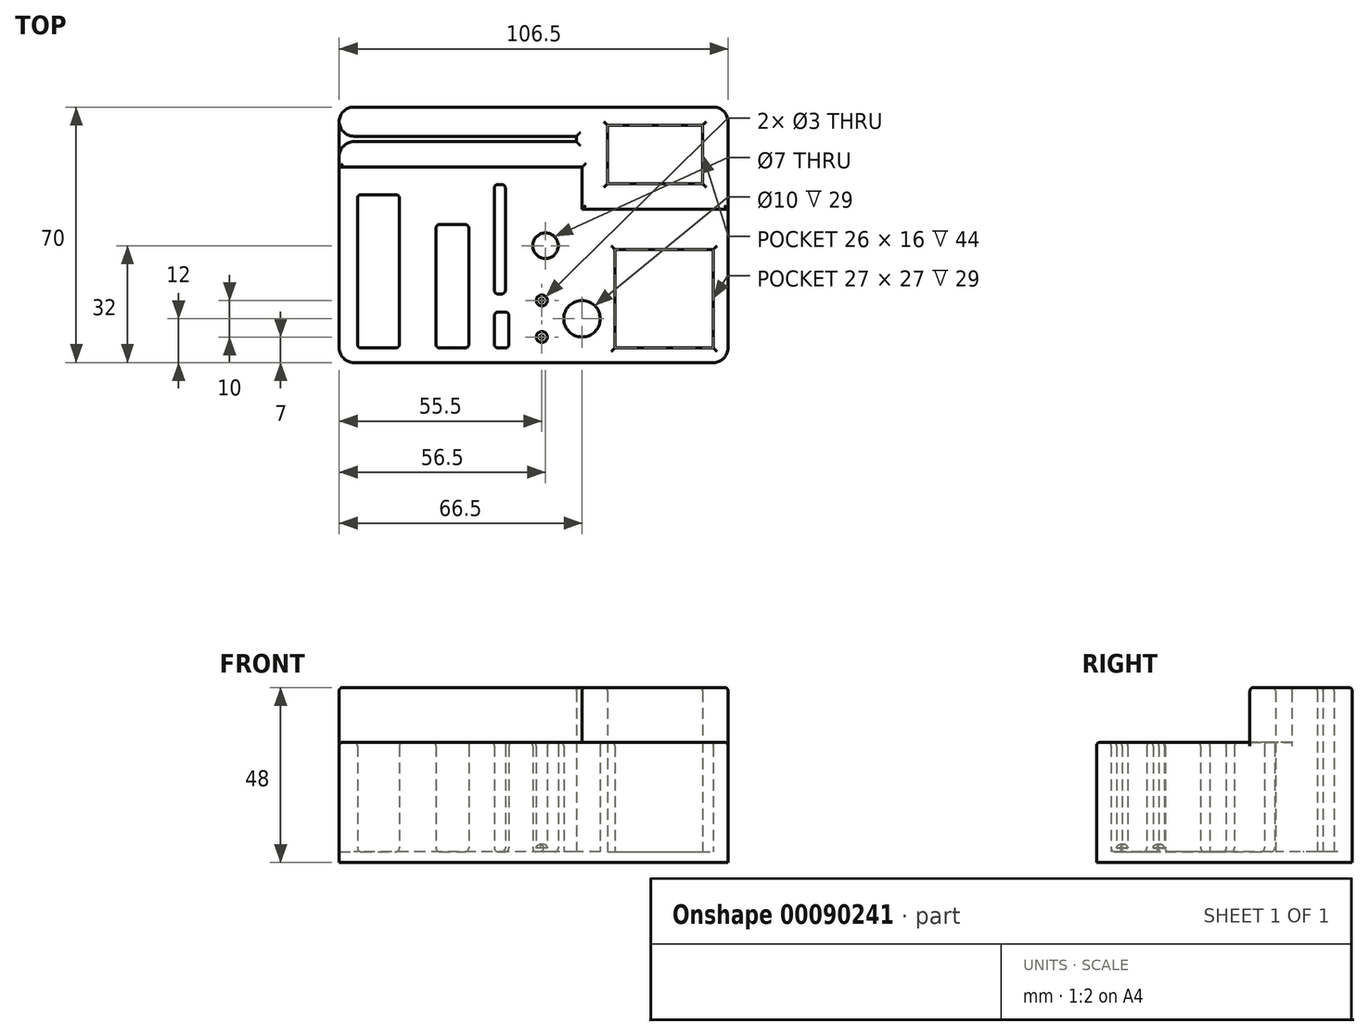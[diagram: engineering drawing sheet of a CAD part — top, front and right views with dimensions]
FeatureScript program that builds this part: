
annotation { "Feature Type Name" : "Feature", "Feature Type Description" : "" }
export const myFeature = defineFeature(function(context is Context, id is Id, definition is map)
    precondition{}
    {
        {
            var Q0;
            Q0=qCreatedBy(makeId("Top.planeOp"),FACE);
            var sketch = newSketch(context, id + "F0", { "sketchPlane" : qUnion([Q0])});
            skLineSegment(sketch, "E0.bottom", {"start": v(-53.25, 35) * mm, "end": v(53.25, 35) * mm});
            skLineSegment(sketch, "E0.top", {"start": v(-53.25, -35) * mm, "end": v(53.25, -35) * mm});
            skLineSegment(sketch, "E0.left", {"start": v(-53.25, 35) * mm, "end": v(-53.25, -35) * mm});
            skLineSegment(sketch, "E0.right", {"start": v(53.25, 35) * mm, "end": v(53.25, -35) * mm});
            skPoint(sketch, "E0.middle", {"position": v(0, 0) * mm});
            skSolve(sketch);
        }
        {
            var Q0;
            Q0 = qSketchRegion(id + "F0", true);
            extrude(context, id + "F1", {"entities" : qUnion([Q0]), "depth" : 3 * mm});
        }
        {
            var Q0;
            Q0=makeQuery(id+"F1.opExtrude","CAP_FACE",FACE,{"disambiguationData":[OSD([sQuery(id+"F0.wireOp",EDGE,"E0.bottom"),sQuery(id+"F0.wireOp",EDGE,"E0.top"),sQuery(id+"F0.wireOp",EDGE,"E0.left"),sQuery(id+"F0.wireOp",EDGE,"E0.right")])],"isStart":false});
            var sketch = newSketch(context, id + "F2", { "sketchPlane" : qUnion([Q0])});
            skLineSegment(sketch, "E1", {"start": v(-53.25, 27) * mm, "end": v(11.75, 27) * mm});
            skLineSegment(sketch, "E2", {"start": v(11.75, 27) * mm, "end": v(11.75, 25.5) * mm});
            skLineSegment(sketch, "E3", {"start": v(11.75, 25.5) * mm, "end": v(-53.25, 25.5) * mm});
            skLineSegment(sketch, "E4", {"start": v(-53.25, 27) * mm, "end": v(-53.25, 35) * mm});
            skLineSegment(sketch, "E5", {"start": v(-53.25, 35) * mm, "end": v(53.25, 35) * mm});
            skLineSegment(sketch, "E6", {"start": v(53.25, 35) * mm, "end": v(53.25, -35) * mm});
            skLineSegment(sketch, "E7", {"start": v(53.25, -35) * mm, "end": v(-53.25, -35) * mm});
            skLineSegment(sketch, "E8", {"start": v(-53.25, -35) * mm, "end": v(-53.25, 25.5) * mm});
            skLineSegment(sketch, "E9.bottom", {"start": v(-48.25, -31) * mm, "end": v(-36.75, -31) * mm});
            skLineSegment(sketch, "E9.top", {"start": v(-48.25, 11) * mm, "end": v(-36.75, 11) * mm});
            skLineSegment(sketch, "E9.left", {"start": v(-48.25, -31) * mm, "end": v(-48.25, 11) * mm});
            skLineSegment(sketch, "E9.right", {"start": v(-36.75, -31) * mm, "end": v(-36.75, 11) * mm});
            skLineSegment(sketch, "E10.bottom", {"start": v(-26.75, -31) * mm, "end": v(-17.75, -31) * mm});
            skLineSegment(sketch, "E10.top", {"start": v(-26.75, 2.8) * mm, "end": v(-17.75, 2.8) * mm});
            skLineSegment(sketch, "E10.left", {"start": v(-26.75, -31) * mm, "end": v(-26.75, 2.8) * mm});
            skLineSegment(sketch, "E10.right", {"start": v(-17.75, -31) * mm, "end": v(-17.75, 2.8) * mm});
            skLineSegment(sketch, "E11.bottom", {"start": v(-10.75, 13.8) * mm, "end": v(-7.75, 13.8) * mm});
            skLineSegment(sketch, "E11.top", {"start": v(-10.75, -16.2) * mm, "end": v(-7.75, -16.2) * mm});
            skLineSegment(sketch, "E11.left", {"start": v(-10.75, 13.8) * mm, "end": v(-10.75, -16.2) * mm});
            skLineSegment(sketch, "E11.right", {"start": v(-7.75, 13.8) * mm, "end": v(-7.75, -16.2) * mm});
            skLineSegment(sketch, "E12.bottom", {"start": v(-10.75, -31) * mm, "end": v(-6.75, -31) * mm});
            skLineSegment(sketch, "E12.top", {"start": v(-10.75, -21.2) * mm, "end": v(-6.75, -21.2) * mm});
            skLineSegment(sketch, "E12.left", {"start": v(-10.75, -31) * mm, "end": v(-10.75, -21.2) * mm});
            skLineSegment(sketch, "E12.right", {"start": v(-6.75, -31) * mm, "end": v(-6.75, -21.2) * mm});
            skCircle(sketch, "E13", {"center": v(3.25, -3) * mm, "radius": 3.5 * mm});
            skCircle(sketch, "E14", {"center": v(2.25, -18) * mm, "radius": 1.5 * mm});
            skCircle(sketch, "E15", {"center": v(2.25, -28) * mm, "radius": 1.5 * mm});
            skLineSegment(sketch, "E16.bottom", {"start": v(22.25, -4) * mm, "end": v(49.25, -4) * mm});
            skLineSegment(sketch, "E16.top", {"start": v(22.25, -31) * mm, "end": v(49.25, -31) * mm});
            skLineSegment(sketch, "E16.left", {"start": v(22.25, -4) * mm, "end": v(22.25, -31) * mm});
            skLineSegment(sketch, "E16.right", {"start": v(49.25, -4) * mm, "end": v(49.25, -31) * mm});
            skLineSegment(sketch, "E17.bottom", {"start": v(20.25, 30) * mm, "end": v(46.25, 30) * mm});
            skLineSegment(sketch, "E17.top", {"start": v(20.25, 14) * mm, "end": v(46.25, 14) * mm});
            skLineSegment(sketch, "E17.left", {"start": v(20.25, 30) * mm, "end": v(20.25, 14) * mm});
            skLineSegment(sketch, "E17.right", {"start": v(46.25, 30) * mm, "end": v(46.25, 14) * mm});
            skCircle(sketch, "E18", {"center": v(13.25, -23) * mm, "radius": 5 * mm});
            skLineSegment(sketch, "E19", {"start": v(53.25, 7) * mm, "end": v(13.25, 7) * mm});
            skLineSegment(sketch, "E20", {"start": v(13.25, 7) * mm, "end": v(13.25, 18.5) * mm});
            skLineSegment(sketch, "E21", {"start": v(13.25, 18.5) * mm, "end": v(-53.25, 18.5) * mm});
            skSolve(sketch);
        }
        {
            var Q0;
            {var subQ0=sQuery(id+"F2.wireOp",EDGE,"E7");Q0=makeQuery(id+"F2.imprint","IMPRINT",FACE,{"disambiguationData":[TD([[makeQuery(id+"F2.imprint","IMPRINT",EDGE,{"derivedFrom":subQ0}),1.0]])]});}
            extrude(context, id + "F3", {"entities" : qUnion([Q0]), "operationType" : NewBodyOperationType.ADD, "depth" : 30 * mm});
        }
        {
            var Q0;
            Q0=makeQuery(id+"F2.imprint","IMPRINT",FACE,{"disambiguationData":[TD([[makeQuery(id+"F2.imprint","IMPRINT",EDGE,{"derivedFrom":sQuery(id+"F2.wireOp",EDGE,"E1")}),1.0]])]});
            extrude(context, id + "F4", {"entities" : qUnion([Q0]), "operationType" : NewBodyOperationType.ADD, "depth" : 45 * mm});
        }
        {
            var Q0;
            Q0=makeQuery(id+"F3.opExtrude","CAP_EDGE",EDGE,{"disambiguationData":[OSD([sQuery(id+"F2.wireOp",EDGE,"E18")])],"isStart":false});
            var Q1;
            Q1=makeQuery(id+"F3.opExtrude","CAP_EDGE",EDGE,{"disambiguationData":[OSD([sQuery(id+"F2.wireOp",EDGE,"E16.bottom")])],"isStart":false});
            var Q2;
            Q2=makeQuery(id+"F3.opExtrude","CAP_EDGE",EDGE,{"disambiguationData":[OSD([sQuery(id+"F2.wireOp",EDGE,"E16.left")])],"isStart":false});
            var Q3;
            Q3=makeQuery(id+"F3.opExtrude","CAP_EDGE",EDGE,{"disambiguationData":[OSD([sQuery(id+"F2.wireOp",EDGE,"E16.right")])],"isStart":false});
            var Q4;
            Q4=makeQuery(id+"F3.opExtrude","CAP_EDGE",EDGE,{"disambiguationData":[OSD([sQuery(id+"F2.wireOp",EDGE,"E16.top")])],"isStart":false});
            var Q5;
            Q5=makeQuery(id+"F3.opExtrude","CAP_EDGE",EDGE,{"disambiguationData":[OSD([sQuery(id+"F2.wireOp",EDGE,"E14")])],"isStart":false});
            var Q6;
            Q6=makeQuery(id+"F3.opExtrude","CAP_EDGE",EDGE,{"disambiguationData":[OSD([sQuery(id+"F2.wireOp",EDGE,"E13")])],"isStart":false});
            var Q7;
            Q7=makeQuery(id+"F3.opExtrude","CAP_EDGE",EDGE,{"disambiguationData":[OSD([sQuery(id+"F2.wireOp",EDGE,"E15")])],"isStart":false});
            var Q8;
            Q8=makeQuery(id+"F3.opExtrude","CAP_EDGE",EDGE,{"disambiguationData":[OSD([sQuery(id+"F2.wireOp",EDGE,"E13")])],"isStart":true});
            var Q9;
            Q9=makeQuery(id+"F3.opExtrude","CAP_EDGE",EDGE,{"disambiguationData":[OSD([sQuery(id+"F2.wireOp",EDGE,"E15")])],"isStart":true});
            var Q10;
            Q10=makeQuery(id+"F3.opExtrude","CAP_EDGE",EDGE,{"disambiguationData":[OSD([sQuery(id+"F2.wireOp",EDGE,"E14")])],"isStart":true});
            var Q11;
            Q11=makeQuery(id+"F3.opExtrude","CAP_EDGE",EDGE,{"disambiguationData":[OSD([sQuery(id+"F2.wireOp",EDGE,"E11.right")])],"isStart":false});
            var Q12;
            Q12=makeQuery(id+"F3.opExtrude","CAP_EDGE",EDGE,{"disambiguationData":[OSD([sQuery(id+"F2.wireOp",EDGE,"E12.right")])],"isStart":false});
            var Q13;
            Q13=makeQuery(id+"F3.opExtrude","CAP_EDGE",EDGE,{"disambiguationData":[OSD([sQuery(id+"F2.wireOp",EDGE,"E11.left")])],"isStart":false});
            var Q14;
            Q14=makeQuery(id+"F3.opExtrude","CAP_EDGE",EDGE,{"disambiguationData":[OSD([sQuery(id+"F2.wireOp",EDGE,"E12.left")])],"isStart":false});
            var Q15;
            Q15=makeQuery(id+"F3.opExtrude","CAP_EDGE",EDGE,{"disambiguationData":[OSD([sQuery(id+"F2.wireOp",EDGE,"E11.bottom")])],"isStart":false});
            var Q16;
            Q16=makeQuery(id+"F3.opExtrude","SWEPT_EDGE",EDGE,{"disambiguationData":[OSD([sQuery(id+"F2.wireOp",EDGE,"E12.top"),sQuery(id+"F2.wireOp",EDGE,"E12.right")])]});
            var Q17;
            Q17=makeQuery(id+"F3.opExtrude","SWEPT_EDGE",EDGE,{"disambiguationData":[OSD([sQuery(id+"F2.wireOp",EDGE,"E11.top"),sQuery(id+"F2.wireOp",EDGE,"E11.right")])]});
            var Q18;
            Q18=makeQuery(id+"F3.opExtrude","CAP_EDGE",EDGE,{"disambiguationData":[OSD([sQuery(id+"F2.wireOp",EDGE,"E12.bottom")])],"isStart":false});
            var Q19;
            Q19=makeQuery(id+"F3.opExtrude","SWEPT_EDGE",EDGE,{"disambiguationData":[OSD([sQuery(id+"F2.wireOp",EDGE,"E12.top"),sQuery(id+"F2.wireOp",EDGE,"E12.left")])]});
            var Q20;
            Q20=makeQuery(id+"F3.opExtrude","CAP_EDGE",EDGE,{"disambiguationData":[OSD([sQuery(id+"F2.wireOp",EDGE,"E11.top")])],"isStart":false});
            var Q21;
            Q21=makeQuery(id+"F3.opExtrude","CAP_EDGE",EDGE,{"disambiguationData":[OSD([sQuery(id+"F2.wireOp",EDGE,"E12.top")])],"isStart":false});
            var Q22;
            Q22=makeQuery(id+"F3.opExtrude","CAP_EDGE",EDGE,{"disambiguationData":[OSD([sQuery(id+"F2.wireOp",EDGE,"E11.right")])],"isStart":true});
            var Q23;
            Q23=makeQuery(id+"F3.opExtrude","CAP_EDGE",EDGE,{"disambiguationData":[OSD([sQuery(id+"F2.wireOp",EDGE,"E12.bottom")])],"isStart":true});
            var Q24;
            Q24=makeQuery(id+"F3.opExtrude","SWEPT_EDGE",EDGE,{"disambiguationData":[OSD([sQuery(id+"F2.wireOp",EDGE,"E12.bottom"),sQuery(id+"F2.wireOp",EDGE,"E12.left")])]});
            var Q25;
            Q25=makeQuery(id+"F3.opExtrude","CAP_EDGE",EDGE,{"disambiguationData":[OSD([sQuery(id+"F2.wireOp",EDGE,"E12.top")])],"isStart":true});
            var Q26;
            Q26=makeQuery(id+"F3.opExtrude","SWEPT_EDGE",EDGE,{"disambiguationData":[OSD([sQuery(id+"F2.wireOp",EDGE,"E12.bottom"),sQuery(id+"F2.wireOp",EDGE,"E12.right")])]});
            var Q27;
            Q27=makeQuery(id+"F3.opExtrude","CAP_EDGE",EDGE,{"disambiguationData":[OSD([sQuery(id+"F2.wireOp",EDGE,"E12.left")])],"isStart":true});
            var Q28;
            Q28=makeQuery(id+"F3.opExtrude","CAP_EDGE",EDGE,{"disambiguationData":[OSD([sQuery(id+"F2.wireOp",EDGE,"E11.bottom")])],"isStart":true});
            var Q29;
            Q29=makeQuery(id+"F3.opExtrude","SWEPT_EDGE",EDGE,{"disambiguationData":[OSD([sQuery(id+"F2.wireOp",EDGE,"E11.top"),sQuery(id+"F2.wireOp",EDGE,"E11.left")])]});
            var Q30;
            Q30=makeQuery(id+"F3.opExtrude","SWEPT_EDGE",EDGE,{"disambiguationData":[OSD([sQuery(id+"F2.wireOp",EDGE,"E11.bottom"),sQuery(id+"F2.wireOp",EDGE,"E11.right")])]});
            var Q31;
            Q31=makeQuery(id+"F3.opExtrude","CAP_EDGE",EDGE,{"disambiguationData":[OSD([sQuery(id+"F2.wireOp",EDGE,"E11.left")])],"isStart":true});
            var Q32;
            Q32=makeQuery(id+"F3.opExtrude","SWEPT_EDGE",EDGE,{"disambiguationData":[OSD([sQuery(id+"F2.wireOp",EDGE,"E11.bottom"),sQuery(id+"F2.wireOp",EDGE,"E11.left")])]});
            var Q33;
            Q33=makeQuery(id+"F3.opExtrude","CAP_EDGE",EDGE,{"disambiguationData":[OSD([sQuery(id+"F2.wireOp",EDGE,"E12.right")])],"isStart":true});
            var Q34;
            Q34=makeQuery(id+"F3.opExtrude","CAP_EDGE",EDGE,{"disambiguationData":[OSD([sQuery(id+"F2.wireOp",EDGE,"E11.top")])],"isStart":true});
            var Q35;
            Q35=makeQuery(id+"F3.opExtrude","CAP_EDGE",EDGE,{"disambiguationData":[OSD([sQuery(id+"F2.wireOp",EDGE,"E10.right")])],"isStart":false});
            var Q36;
            Q36=makeQuery(id+"F3.opExtrude","CAP_EDGE",EDGE,{"disambiguationData":[OSD([sQuery(id+"F2.wireOp",EDGE,"E10.left")])],"isStart":false});
            var Q37;
            Q37=makeQuery(id+"F3.opExtrude","CAP_EDGE",EDGE,{"disambiguationData":[OSD([sQuery(id+"F2.wireOp",EDGE,"E10.bottom")])],"isStart":false});
            var Q38;
            Q38=makeQuery(id+"F3.opExtrude","CAP_EDGE",EDGE,{"disambiguationData":[OSD([sQuery(id+"F2.wireOp",EDGE,"E10.top")])],"isStart":false});
            var Q39;
            Q39=makeQuery(id+"F3.opExtrude","CAP_EDGE",EDGE,{"disambiguationData":[OSD([sQuery(id+"F2.wireOp",EDGE,"E10.right")])],"isStart":true});
            var Q40;
            Q40=makeQuery(id+"F3.opExtrude","CAP_EDGE",EDGE,{"disambiguationData":[OSD([sQuery(id+"F2.wireOp",EDGE,"E10.left")])],"isStart":true});
            var Q41;
            Q41=makeQuery(id+"F3.opExtrude","SWEPT_EDGE",EDGE,{"disambiguationData":[OSD([sQuery(id+"F2.wireOp",EDGE,"E10.top"),sQuery(id+"F2.wireOp",EDGE,"E10.left")])]});
            var Q42;
            Q42=makeQuery(id+"F3.opExtrude","SWEPT_EDGE",EDGE,{"disambiguationData":[OSD([sQuery(id+"F2.wireOp",EDGE,"E10.bottom"),sQuery(id+"F2.wireOp",EDGE,"E10.right")])]});
            var Q43;
            Q43=makeQuery(id+"F3.opExtrude","SWEPT_EDGE",EDGE,{"disambiguationData":[OSD([sQuery(id+"F2.wireOp",EDGE,"E10.bottom"),sQuery(id+"F2.wireOp",EDGE,"E10.left")])]});
            var Q44;
            Q44=makeQuery(id+"F3.opExtrude","CAP_EDGE",EDGE,{"disambiguationData":[OSD([sQuery(id+"F2.wireOp",EDGE,"E10.bottom")])],"isStart":true});
            var Q45;
            Q45=makeQuery(id+"F3.opExtrude","CAP_EDGE",EDGE,{"disambiguationData":[OSD([sQuery(id+"F2.wireOp",EDGE,"E10.top")])],"isStart":true});
            var Q46;
            Q46=makeQuery(id+"F3.opExtrude","SWEPT_EDGE",EDGE,{"disambiguationData":[OSD([sQuery(id+"F2.wireOp",EDGE,"E10.top"),sQuery(id+"F2.wireOp",EDGE,"E10.right")])]});
            var Q47;
            Q47=makeQuery(id+"F3.opExtrude","CAP_EDGE",EDGE,{"disambiguationData":[OSD([sQuery(id+"F2.wireOp",EDGE,"E9.right")])],"isStart":false});
            var Q48;
            Q48=makeQuery(id+"F3.opExtrude","CAP_EDGE",EDGE,{"disambiguationData":[OSD([sQuery(id+"F2.wireOp",EDGE,"E9.left")])],"isStart":false});
            var Q49;
            Q49=makeQuery(id+"F3.opExtrude","CAP_EDGE",EDGE,{"disambiguationData":[OSD([sQuery(id+"F2.wireOp",EDGE,"E9.bottom")])],"isStart":false});
            var Q50;
            Q50=makeQuery(id+"F3.opExtrude","CAP_EDGE",EDGE,{"disambiguationData":[OSD([sQuery(id+"F2.wireOp",EDGE,"E9.top")])],"isStart":false});
            var Q51;
            Q51=makeQuery(id+"F3.opExtrude","CAP_EDGE",EDGE,{"disambiguationData":[OSD([sQuery(id+"F2.wireOp",EDGE,"E9.right")])],"isStart":true});
            var Q52;
            Q52=makeQuery(id+"F3.opExtrude","CAP_EDGE",EDGE,{"disambiguationData":[OSD([sQuery(id+"F2.wireOp",EDGE,"E9.left")])],"isStart":true});
            var Q53;
            Q53=makeQuery(id+"F3.opExtrude","SWEPT_EDGE",EDGE,{"disambiguationData":[OSD([sQuery(id+"F2.wireOp",EDGE,"E9.top"),sQuery(id+"F2.wireOp",EDGE,"E9.left")])]});
            var Q54;
            Q54=makeQuery(id+"F3.opExtrude","SWEPT_EDGE",EDGE,{"disambiguationData":[OSD([sQuery(id+"F2.wireOp",EDGE,"E9.bottom"),sQuery(id+"F2.wireOp",EDGE,"E9.right")])]});
            var Q55;
            Q55=makeQuery(id+"F3.opExtrude","SWEPT_EDGE",EDGE,{"disambiguationData":[OSD([sQuery(id+"F2.wireOp",EDGE,"E9.top"),sQuery(id+"F2.wireOp",EDGE,"E9.right")])]});
            var Q56;
            Q56=makeQuery(id+"F3.opExtrude","SWEPT_EDGE",EDGE,{"disambiguationData":[OSD([sQuery(id+"F2.wireOp",EDGE,"E9.bottom"),sQuery(id+"F2.wireOp",EDGE,"E9.left")])]});
            var Q57;
            Q57=makeQuery(id+"F3.opExtrude","CAP_EDGE",EDGE,{"disambiguationData":[OSD([sQuery(id+"F2.wireOp",EDGE,"E9.top")])],"isStart":true});
            var Q58;
            Q58=makeQuery(id+"F3.opExtrude","CAP_EDGE",EDGE,{"disambiguationData":[OSD([sQuery(id+"F2.wireOp",EDGE,"E9.bottom")])],"isStart":true});
            var Q59;
            Q59=makeQuery(id+"F3.opExtrude","CAP_EDGE",EDGE,{"disambiguationData":[OSD([sQuery(id+"F2.wireOp",EDGE,"E8")])],"isStart":false});
            var Q60;
            Q60=makeQuery(id+"F3.opExtrude","CAP_EDGE",EDGE,{"disambiguationData":[OSD([sQuery(id+"F2.wireOp",EDGE,"E7")])],"isStart":false});
            var Q61;
            Q61=makeQuery(id+"F3.opExtrude","CAP_EDGE",EDGE,{"disambiguationData":[OSD([sQuery(id+"F2.wireOp",EDGE,"E6")])],"isStart":false});
            var Q62;
            Q62=makeQuery(id+"F4.opExtrude","CAP_EDGE",EDGE,{"disambiguationData":[OSD([sQuery(id+"F2.wireOp",EDGE,"E21")])],"isStart":false});
            var Q63;
            Q63=makeQuery(id+"F4.opExtrude","CAP_EDGE",EDGE,{"disambiguationData":[OSD([sQuery(id+"F2.wireOp",EDGE,"E20")])],"isStart":false});
            var Q64;
            Q64=makeQuery(id+"F4.opExtrude","CAP_EDGE",EDGE,{"disambiguationData":[OSD([sQuery(id+"F2.wireOp",EDGE,"E19")])],"isStart":false});
            var Q65;
            Q65=makeQuery(id+"F4.opExtrude","CAP_EDGE",EDGE,{"disambiguationData":[OSD([sQuery(id+"F2.wireOp",EDGE,"E6")])],"isStart":false});
            var Q66;
            Q66=makeQuery(id+"F4.opExtrude","CAP_EDGE",EDGE,{"disambiguationData":[OSD([sQuery(id+"F2.wireOp",EDGE,"E5")])],"isStart":false});
            var Q67;
            Q67=makeQuery(id+"F4.opExtrude","CAP_EDGE",EDGE,{"disambiguationData":[OSD([sQuery(id+"F2.wireOp",EDGE,"E4")])],"isStart":false});
            var Q68;
            Q68=makeQuery(id+"F4.opExtrude","CAP_EDGE",EDGE,{"disambiguationData":[OSD([sQuery(id+"F2.wireOp",EDGE,"E8")])],"isStart":false});
            var Q69;
            Q69=makeQuery(id+"F4.opExtrude","CAP_FACE",FACE,{"disambiguationData":[OSD([sQuery(id+"F2.wireOp",EDGE,"E1"),sQuery(id+"F2.wireOp",EDGE,"E2"),sQuery(id+"F2.wireOp",EDGE,"E3"),sQuery(id+"F2.wireOp",EDGE,"E4"),sQuery(id+"F2.wireOp",EDGE,"E5"),sQuery(id+"F2.wireOp",EDGE,"E6"),sQuery(id+"F2.wireOp",EDGE,"E8"),sQuery(id+"F2.wireOp",EDGE,"E17.bottom"),sQuery(id+"F2.wireOp",EDGE,"E17.top"),sQuery(id+"F2.wireOp",EDGE,"E17.left"),sQuery(id+"F2.wireOp",EDGE,"E17.right"),sQuery(id+"F2.wireOp",EDGE,"E19"),sQuery(id+"F2.wireOp",EDGE,"E20"),sQuery(id+"F2.wireOp",EDGE,"E21")])],"isStart":false});
            fillet(context, id + "F5", {"entities" : qUnion([Q0, Q1, Q2, Q3, Q4, Q5, Q6, Q7, Q8, Q9, Q10, Q11, Q12, Q13, Q14, Q15, Q16, Q17, Q18, Q19, Q20, Q21, Q22, Q23, Q24, Q25, Q26, Q27, Q28, Q29, Q30, Q31, Q32, Q33, Q34, Q35, Q36, Q37, Q38, Q39, Q40, Q41, Q42, Q43, Q44, Q45, Q46, Q47, Q48, Q49, Q50, Q51, Q52, Q53, Q54, Q55, Q56, Q57, Q58, Q59, Q60, Q61, Q62, Q63, Q64, Q65, Q66, Q67, Q68, Q69]), "radius" : 1 * mm, "tangentPropagation" : true, "allowEdgeOverflow" : false});
        }
        {
            var Q0;
            Q0=makeQuery(id+"F3.boolean.opBoolean","MERGE",EDGE,{"derivedFrom":[makeQuery(id+"F1.opExtrude","SWEPT_EDGE",EDGE,{"disambiguationData":[OSD([sQuery(id+"F0.wireOp",EDGE,"E0.top"),sQuery(id+"F0.wireOp",EDGE,"E0.right")])]}),makeQuery(id+"F3.opExtrude","SWEPT_EDGE",EDGE,{"disambiguationData":[OSD([sQuery(id+"F2.wireOp",EDGE,"E6"),sQuery(id+"F2.wireOp",EDGE,"E7")])]})]});
            var Q1;
            Q1=makeQuery(id+"F3.boolean.opBoolean","MERGE",EDGE,{"derivedFrom":[makeQuery(id+"F1.opExtrude","SWEPT_EDGE",EDGE,{"disambiguationData":[OSD([sQuery(id+"F0.wireOp",EDGE,"E0.top"),sQuery(id+"F0.wireOp",EDGE,"E0.left")])]}),makeQuery(id+"F3.opExtrude","SWEPT_EDGE",EDGE,{"disambiguationData":[OSD([sQuery(id+"F2.wireOp",EDGE,"E7"),sQuery(id+"F2.wireOp",EDGE,"E8")])]})]});
            var Q2;
            Q2=makeQuery(id+"F3.boolean.opBoolean","MERGE",EDGE,{"derivedFrom":[makeQuery(id+"F1.opExtrude","SWEPT_EDGE",EDGE,{"disambiguationData":[OSD([sQuery(id+"F0.wireOp",EDGE,"E0.bottom"),sQuery(id+"F0.wireOp",EDGE,"E0.left")])]}),makeQuery(id+"F3.opExtrude","SWEPT_EDGE",EDGE,{"disambiguationData":[OSD([sQuery(id+"F2.wireOp",EDGE,"E4"),sQuery(id+"F2.wireOp",EDGE,"E5")])]})]});
            var Q3;
            Q3=makeQuery(id+"F3.boolean.opBoolean","MERGE",EDGE,{"derivedFrom":[makeQuery(id+"F1.opExtrude","SWEPT_EDGE",EDGE,{"disambiguationData":[OSD([sQuery(id+"F0.wireOp",EDGE,"E0.bottom"),sQuery(id+"F0.wireOp",EDGE,"E0.right")])]}),makeQuery(id+"F3.opExtrude","SWEPT_EDGE",EDGE,{"disambiguationData":[OSD([sQuery(id+"F2.wireOp",EDGE,"E5"),sQuery(id+"F2.wireOp",EDGE,"E6")])]})]});
            var Q4;
            Q4=makeQuery(id+"F4.opExtrude","SWEPT_EDGE",EDGE,{"disambiguationData":[OSD([sQuery(id+"F0.wireOp",EDGE,"E0.left"),sQuery(id+"F2.wireOp",EDGE,"E3"),sQuery(id+"F2.wireOp",EDGE,"E8")])]});
            var Q5;
            Q5=makeQuery(id+"F4.opExtrude","SWEPT_EDGE",EDGE,{"disambiguationData":[OSD([sQuery(id+"F0.wireOp",EDGE,"E0.left"),sQuery(id+"F2.wireOp",EDGE,"E1"),sQuery(id+"F2.wireOp",EDGE,"E4")])]});
            var Q6;
            Q6=makeQuery(id+"F4.boolean.opBoolean","MERGE",EDGE,{"derivedFrom":[makeQuery(id+"F1.opExtrude","SWEPT_EDGE",EDGE,{"disambiguationData":[OSD([sQuery(id+"F0.wireOp",EDGE,"E0.bottom"),sQuery(id+"F0.wireOp",EDGE,"E0.left")])]}),makeQuery(id+"F4.opExtrude","SWEPT_EDGE",EDGE,{"disambiguationData":[OSD([sQuery(id+"F2.wireOp",EDGE,"E4"),sQuery(id+"F2.wireOp",EDGE,"E5")])]})]});
            var Q7;
            Q7=makeQuery(id+"F4.boolean.opBoolean","MERGE",EDGE,{"derivedFrom":[makeQuery(id+"F1.opExtrude","SWEPT_EDGE",EDGE,{"disambiguationData":[OSD([sQuery(id+"F0.wireOp",EDGE,"E0.bottom"),sQuery(id+"F0.wireOp",EDGE,"E0.right")])]}),makeQuery(id+"F4.opExtrude","SWEPT_EDGE",EDGE,{"disambiguationData":[OSD([sQuery(id+"F2.wireOp",EDGE,"E5"),sQuery(id+"F2.wireOp",EDGE,"E6")])]})]});
            fillet(context, id + "F6", {"entities" : qUnion([Q0, Q1, Q2, Q3, Q4, Q5, Q6, Q7]), "radius" : 4 * mm, "tangentPropagation" : true, "allowEdgeOverflow" : false});
        }
    });
